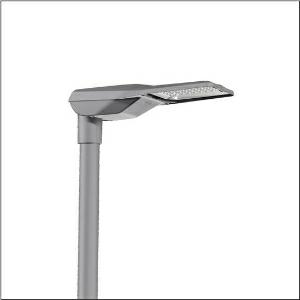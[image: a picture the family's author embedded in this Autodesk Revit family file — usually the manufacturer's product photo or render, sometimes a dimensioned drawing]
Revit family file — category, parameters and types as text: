
# Revit family: streetlight_sl_21_iq_mini___p0_8ab_5xe2r31g08jb_270d
name_source: partatom
category: Lighting Fixtures
units: mm (PartAtom-declared; Revit-internal decimal feet)

## family parameters
Cut with Voids When Loaded = No
Host = Face
Light Source = No
Part Type = Normal
Room Calculation Point = No
Round Connector Dimension = Use Diameter
Shared = No

## types (1)
- --- (1 x LED, 9400 lm, 71.6 W, 3000K)
    Apparent Load = 72 VA
    CIE Flux Codes = 39 72 97 100 100
    Color Rendering = 70
    Color Temperature = 3000K
    Default Elevation = 1800 mm
    Description = Streetlight SL 21 iQ mini, mast luminaire, primary light control with lens, of PMMA, primary optical cover: cover, of toughened safety glass, transparent, light distribution: P0.8aB, light emission: direct distribution, primary light characteristic: asymmetric, installation type: post-top, side-entry, LED, High Power LED, rated luminous flux: 9.400lm, luminous efficacy: 131lm/W, light colour: 730, colour temperature: 3000K, control gear: iQ Street-Remote, control: pre-setting: linear dimming characteristic, Street-Remote, Auto-Match, Temp-Guard, Lumen-Switch, Night-Set, Smart-Wire, Light-Fading, Desk-Remote (wireless, voltage-free reading and setting of iQ features in the workshop via application-optimized NFC function/RFID function), optimised constant luminous flux control (CLO 2.0), mains connection: 220..240V, AC, 50/60Hz, start of lifetime: 72W, end of service life: 75W, reduction: 33W, luminaire housing, of diecast aluminium, powder-coated, SITECO metallic grey (DB 702S), corrosivity category C5 high according to DIN EN ISO 12944, please order mast flange separately, inclination adjustable: 0°, 5°, 10°, 15°, sealing non-destructively replaceable, multi-level sealing system, length: 628mm, width: 235mm, height: 110mm, mast flange for spigot size: 42mm (side-entry): 5XC10008XM4, 60/48mm (side-entry/post-top): 5XC10108XM2, 76/60mm (side-entry/post-top): 5XC10108XM1, mounting height: 4..8m, protection rating (complete): IP66, insulation class (complete): insulation class II (safety insulation), certification: CE, ENEC, ENEC+, VDE, impact resistance: IK10, permissible operating ambient temperature for outdoor applications: -40..+50°C, standard-compliant lighting for roads and squares, packaging unit: 1 piece

Light Distribution: P0.8aB
    Height = 110 mm
    Lamp = 1 x LED
    Lamp Light Flux = 9400 lm
    Lamp Power = 71.6 W
    Lamp count = 1
    Length = 625 mm
    Luminous efficacy = 131 lm/W
    Manufacturer = Siteco
    ModVariant = No
    Model = 5XE2R31G08JB
    Number of Poles = 1
    OnlyDefault = Yes
    Power Factor = 1
    Product Name = Streetlight SL 21 iQ mini | P0.8aB
    Product group = mast luminaire | pylon top
    ProductGroupID = 6100
    Protection Class = Protection class II
    Protection Degree = IP 66
    RLX_Detail_Level = 1
    RLX_Emergency_Light_Flux = 0 lm
    RLX_Emergency_Type = 0
    RLX_Emergency_Type_DB = No
    RlxData = <blob elided: 91533 chars, md5=d7981476>
    Socket = socket
    Standby Power = 0 W
    System Light Flux = 9400 lm
    System Power = 72 W
    Type Comments = factory setting: luminous flux: 100 % | dim-lin: 254 | 746 mA
    Type Image = l_1003519.jpg
    URL = http://relux.com
    VarID = @adj_078839
    Voltage = 0 V
    Weight = 0.00 kg
    Width = 234 mm

## geometry (parser evidence)
native form markers: Blend x4, Sweep x11
no freeform markers — native parametric forms only
